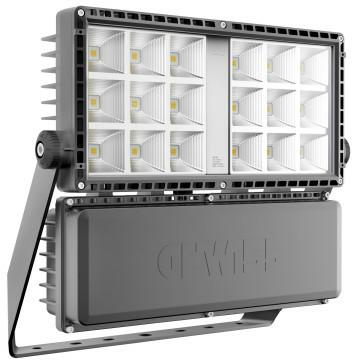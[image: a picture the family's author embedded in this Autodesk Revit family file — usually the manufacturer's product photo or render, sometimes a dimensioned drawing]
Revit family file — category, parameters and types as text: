
# Revit family: Lighting-Proiezione-GEWISS-SMART[PRO]2.0-PROIETTORI-LED-MEDIA-POTENZA_2MODULI_CLI
name_source: partatom
category: Apparecchi per illuminazione
units: mm (PartAtom-declared; Revit-internal decimal feet)

## family parameters
Condiviso = No
Host = Superficie
Punto di calcolo locali = No
Quota connettore circolare = Usa diametro
Sorgente d'illuminazione = No
Taglio con vuoti quando caricato = No
Tipo di parte = Normale

## types (1)
- Lighting-Proiezione-GEWISS-SMART[PRO]2.0-PROIETTORI-LED-MEDIA-POTENZA_2MODULI_CLI
    Alimentatore = Incluso
    Apparecchio a ridotta temperatura superficiale = No
    Applicazione = Interno / Esterno
    Cablaggio = Connettore stagno
    Caratteristiche elettriche e gestione della luce = -
    Caratteristiche ottiche e illuminotecniche = -
    Catalogo = LIGHTING
    Certificazione DIN 18032-3 = Si
    Certificazioni e classificazioni = -
    Classe fotobiologica = -
    Classe isolamento = I
    Classificazione: = -
    Codice digitale univoco (Datamatrix) = Attualmente non presente
    Colore = Grigio grafite
    Contesto = Illuminazione di grandi aree, impianti sportivi
    Controllo abbagliamento e luminanza = G*6 - ULOR = 0
    Corpo = Alluminio pressofuso
    Descrizione = SMARTPRO2.0 2M 5700K CRI80 A3 1-10V CL1
    Dispositivo di protezione = DM 5KV / CM 10KV
    Durata di vita = L90B10 (Tq+25°C) - 40000h L90B10 (Tq+50°C) = 32000h L80B10 (Tq+25°C) - 90000h
    Efficienza luminosa (lm/W) = 113
    Finitura colore = Verniciato a polvere poliestere
    Fissaggio = Staffa
    Frequenza nominale (Hz) = 50 / 60
    GW - Codice Electrocod = 2424
    Gancio di chiusura = Viti metriche esagonali
    Garanzia = 5 anni
    Grado di protezione = IP66
    Gruppo ottico = Parabola in alluminio anodizzato brillantato con alluminio puro 99,99%
    Guarnizioni = silicone antinvecchiamento
    IDF = 311943a0-bd02-467d-a9ed-f2a4dacf2862
    IDT = 94ca63f114e34adea3421514a6ca964f
    IPEA = STRADALE = A // GRANDI AREE = A3+ // CICLOPEDONALI = A+ // AREE VERDI = A+ // CENTRO STORICO = A5+ // ALTRO = A5+
    Immagine tipo = GWP2275AS.jpg
    Inclinazione = Rotazione su staffa con goniometro integrato
    Indice di resa cromatica = CRI-80
    Informazioni generali = -
    Installazione e manutenzione = -
    Lampada = LED
    Lumen output (lm) = 37200
    Materiali = -
    Modello = GWP2285NS
    Norma di riferimento = EN60598-1; EN60598-2-5; IEC 62778; IEC 62471; EN13201
    Ottica = A3 - Asimmetrica Stretta
    Peso (kg): = 13
    Potenza di sistema = 330W
    Produttore = GEWISS S.p.A.
    Prospetto di default = 1219 mm
    Resistenza agli urti = IK08
    Resistenza al filo incandescente = -
    SEO = Proiettore
    Scheda Tecnica = https://www.gewiss.com
    Schermo = Vetro piano extrachiaro spessore 4mm
    Sistema di controllo = Stand Alone - 1/10V
    Sostituibilità gruppo ottico = Non disponibile
    Sostituibilità piastra di cablaggio = Non disponibile
    Spostamento_x = 2186 mm
    Spostamento_x_effettivo = 1814 mm
    Superficie massima esposta al vento : = 0,170 m2
    Temperatura di colore = 5700K
    Temperatura di esercizio = -30 +50 °C
    Temperatura di stoccaggio = -
    Tensione di alimentazione = 220 - 240 V
    Tipo di apparecchio = Apparecchio per proiezione LED di piccola, media e alta potenza
    Tipo di installazione e montaggio = Torrefaro - Parete - Terra
    Tipologia sorgente luminosa = LED - Non sostituibile
    Tolleranza cromatica = SDCM = 3
    URL = https://www.gewiss.com
    Vano di alimentazione = Integrato
    Versione file RFA = 20.11
    Versioni = Luce fredda 5700K
    Viti esterne = Acciaio inossidabile
